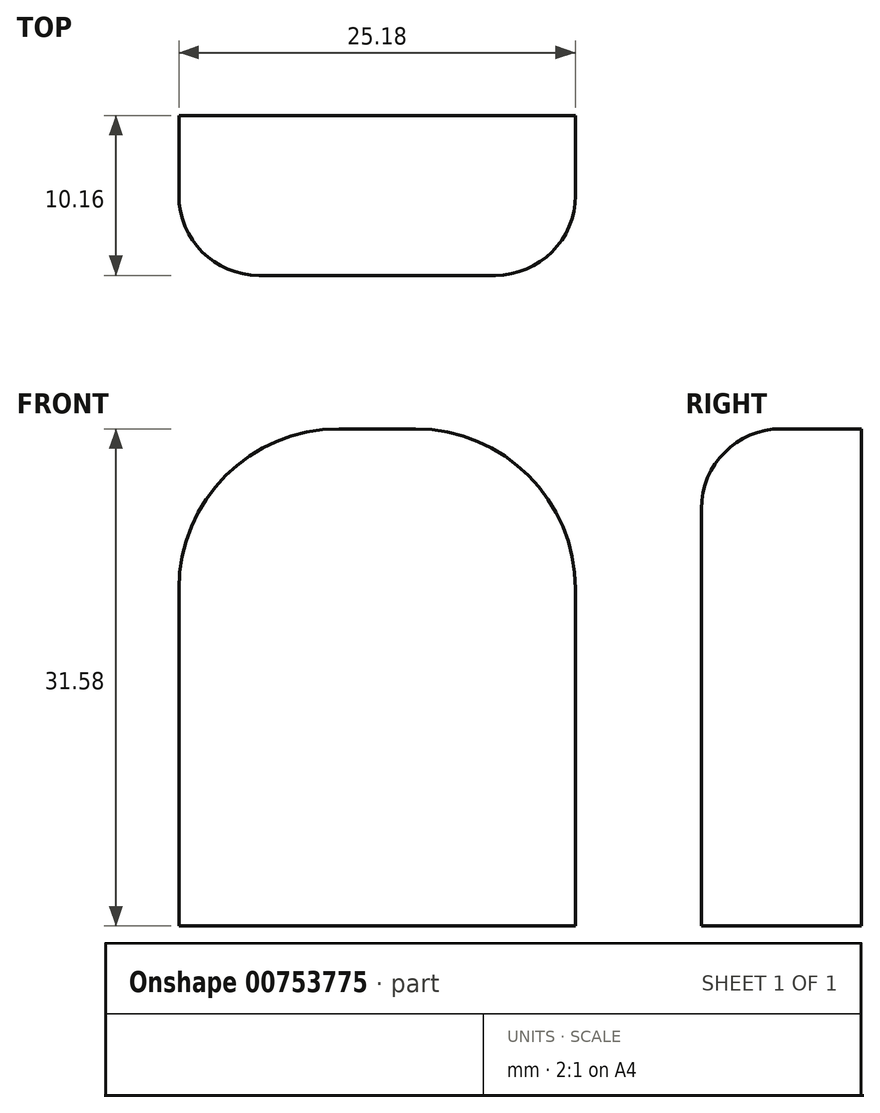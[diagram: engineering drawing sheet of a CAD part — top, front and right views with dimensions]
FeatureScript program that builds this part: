
annotation { "Feature Type Name" : "Feature", "Feature Type Description" : "" }
export const myFeature = defineFeature(function(context is Context, id is Id, definition is map)
    precondition{}
    {
        {
            var Q0;
            Q0=qCreatedBy(makeId("Front.planeOp"),FACE);
            var sketch = newSketch(context, id + "F0", { "sketchPlane" : qUnion([Q0])});
            skLineSegment(sketch, "E0.bottom", {"start": v(12.6, -15.8) * mm, "end": v(-12.6, -15.8) * mm});
            skLineSegment(sketch, "E0.top", {"start": v(2.43, 15.8) * mm, "end": v(-2.43, 15.8) * mm});
            skLineSegment(sketch, "E0.left", {"start": v(12.6, -15.8) * mm, "end": v(12.6, 5.63) * mm});
            skLineSegment(sketch, "E0.right", {"start": v(-12.6, -15.8) * mm, "end": v(-12.6, 5.63) * mm});
            skPoint(sketch, "E0.middle", {"position": v(0, 0) * mm});
            skPoint(sketch, "E1.visualSharp", {"position": v(-12.6, 15.8) * mm});
            skArc(sketch, "E1.filletArc", {"start": v(-2.43, 15.8) * mm, "mid": v(-9.62, 12.82) * mm, "end": v(-12.6, 5.63) * mm});
            skPoint(sketch, "E2.visualSharp", {"position": v(12.6, 15.8) * mm});
            skArc(sketch, "E2.filletArc", {"start": v(12.6, 5.63) * mm, "mid": v(9.62, 12.82) * mm, "end": v(2.43, 15.8) * mm});
            skSolve(sketch);
        }
        {
            var Q0;
            Q0 = qSketchRegion(id + "F0", true);
            extrude(context, id + "F1", {"entities" : qUnion([Q0]), "depth" : 10.16 * mm, "offsetDistance" : 25.4 * mm});
        }
        {
            var Q0;
            Q0=makeQuery(id+"F1.opExtrude","CAP_EDGE",EDGE,{"disambiguationData":[OSD([sQuery(id+"F0.wireOp",EDGE,"E2.filletArc")])],"isStart":false});
            var Q1;
            Q1=makeQuery(id+"F1.opExtrude","CAP_EDGE",EDGE,{"disambiguationData":[OSD([sQuery(id+"F0.wireOp",EDGE,"E0.left")])],"isStart":false});
            fillet(context, id + "F2", {"entities" : qUnion([Q0, Q1]), "radius" : 5.08 * mm, "tangentPropagation" : true, "allowEdgeOverflow" : false});
        }
    });
